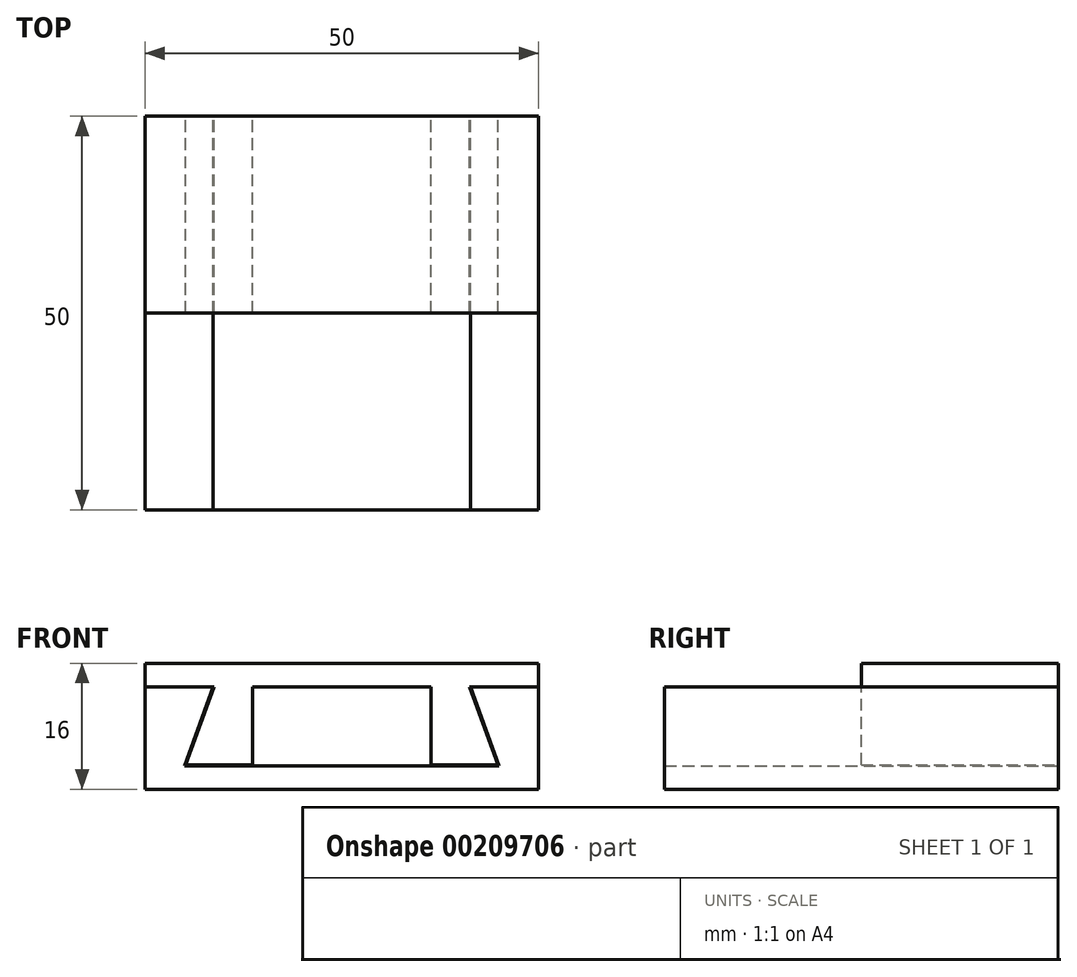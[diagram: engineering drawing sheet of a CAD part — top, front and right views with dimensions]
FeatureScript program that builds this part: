
annotation { "Feature Type Name" : "Feature", "Feature Type Description" : "" }
export const myFeature = defineFeature(function(context is Context, id is Id, definition is map)
    precondition{}
    {
        {
            var Q0;
            Q0=qCreatedBy(makeId("Front.planeOp"),FACE);
            var sketch = newSketch(context, id + "F0", { "sketchPlane" : qUnion([Q0])});
            skLineSegment(sketch, "E0.bottom", {"start": v(0, 0) * mm, "end": v(50, 0) * mm});
            skLineSegment(sketch, "E0.top", {"start": v(0, 3) * mm, "end": v(50, 3) * mm});
            skLineSegment(sketch, "E0.left", {"start": v(0, 0) * mm, "end": v(0, 3) * mm});
            skLineSegment(sketch, "E0.right", {"start": v(50, 0) * mm, "end": v(50, 3) * mm});
            skLineSegment(sketch, "E1", {"start": v(0, 3) * mm, "end": v(0, 13) * mm});
            skLineSegment(sketch, "E2", {"start": v(0, 13) * mm, "end": v(8.64, 13) * mm});
            skLineSegment(sketch, "E3", {"start": v(8.64, 13) * mm, "end": v(5, 3) * mm});
            skPoint(sketch, "E4", {"position": v(25, 0) * mm});
            skLineSegment(sketch, "E5", {"start": v(25, 0) * mm, "end": v(25, 29.58) * mm, "construction": true});
            skLineSegment(sketch, "E6.MirrorCS", {"start": v(41.36, 13) * mm, "end": v(45, 3) * mm});
            skLineSegment(sketch, "E7.MirrorCS", {"start": v(50, 13) * mm, "end": v(41.36, 13) * mm});
            skLineSegment(sketch, "E8.MirrorCS", {"start": v(50, 3) * mm, "end": v(50, 13) * mm});
            skLineSegment(sketch, "E9.MirrorCS", {"start": v(50, 3) * mm, "end": v(0, 3) * mm});
            skPoint(sketch, "E10", {"position": v(5, 3) * mm});
            skPoint(sketch, "E11", {"position": v(45, 3) * mm});
            skLineSegment(sketch, "E12", {"start": v(0, 13) * mm, "end": v(0, 16) * mm});
            skLineSegment(sketch, "E13", {"start": v(0, 16) * mm, "end": v(50, 16) * mm});
            skLineSegment(sketch, "E14", {"start": v(50, 16) * mm, "end": v(50, 13) * mm});
            skLineSegment(sketch, "E15", {"start": v(8.64, 13) * mm, "end": v(41.36, 13) * mm});
            skLineSegment(sketch, "E16", {"start": v(13.64, 13) * mm, "end": v(13.64, 3) * mm});
            skPoint(sketch, "E17", {"position": v(13.64, 13) * mm});
            skLineSegment(sketch, "E18.MirrorCS", {"start": v(36.36, 13) * mm, "end": v(36.36, 3) * mm});
            skLineSegment(sketch, "E19.0", {"start": v(41.27, 12.97) * mm, "end": v(44.9, 2.97) * mm});
            skLineSegment(sketch, "E20.0", {"start": v(0, -5) * mm, "end": v(50, -5) * mm});
            skLineSegment(sketch, "E21", {"start": v(41.27, 12.97) * mm, "end": v(41.25, 13) * mm});
            skLineSegment(sketch, "E22.0", {"start": v(50, 3.1) * mm, "end": v(0, 3.1) * mm});
            skPoint(sketch, "E23", {"position": v(44.86, 3.1) * mm});
            skLineSegment(sketch, "E24.MirrorCS", {"start": v(8.73, 12.97) * mm, "end": v(5.1, 2.97) * mm});
            skPoint(sketch, "E25", {"position": v(5.14, 3.1) * mm});
            skLineSegment(sketch, "E26", {"start": v(8.73, 12.97) * mm, "end": v(8.75, 13) * mm});
            skSolve(sketch);
        }
        {
            var Q0;
            {var subQ0=sQuery(id+"F0.wireOp",EDGE,"E1");Q0=makeQuery(id+"F0.imprint","IMPRINT",FACE,{"disambiguationData":[TD([[makeQuery(id+"F0.imprint","IMPRINT",EDGE,{"derivedFrom":subQ0}),-1.0]])]});}
            var Q1;
            Q1=makeQuery(id+"F0.imprint","IMPRINT",FACE,{"disambiguationData":[TD([[makeQuery(id+"F0.imprint","IMPRINT",EDGE,{"derivedFrom":sQuery(id+"F0.wireOp",EDGE,"E0.bottom")}),1.0]])]});
            var Q2;
            {var subQ0=sQuery(id+"F0.wireOp",EDGE,"E6.MirrorCS");Q2=makeQuery(id+"F0.imprint","IMPRINT",FACE,{"disambiguationData":[TD([[makeQuery(id+"F0.imprint","IMPRINT",EDGE,{"derivedFrom":subQ0}),1.0]])]});}
            extrude(context, id + "F1", {"entities" : qUnion([Q0, Q1, Q2]), "depth" : 50 * mm});
        }
        {
            var Q0;
            {var subQ3=sQuery(id+"F0.wireOp",EDGE,"E2");Q0=makeQuery(id+"F0.imprint","IMPRINT",FACE,{"disambiguationData":[TD([[makeQuery(id+"F0.imprint","IMPRINT",EDGE,{"derivedFrom":subQ3}),1.0]])]});}
            var Q1;
            {var subQ5=sQuery(id+"F0.wireOp",EDGE,"E26");Q1=makeQuery(id+"F0.imprint","IMPRINT",FACE,{"disambiguationData":[TD([[makeQuery(id+"F0.imprint","IMPRINT",EDGE,{"derivedFrom":subQ5}),-1.0]])]});}
            var Q2;
            {var subQ0=sQuery(id+"F0.wireOp",EDGE,"E21");Q2=makeQuery(id+"F0.imprint","IMPRINT",FACE,{"disambiguationData":[TD([[makeQuery(id+"F0.imprint","IMPRINT",EDGE,{"derivedFrom":subQ0}),1.0]])]});}
            extrude(context, id + "F2", {"entities" : qUnion([Q0, Q1, Q2]), "depth" : 25 * mm});
        }
    });
